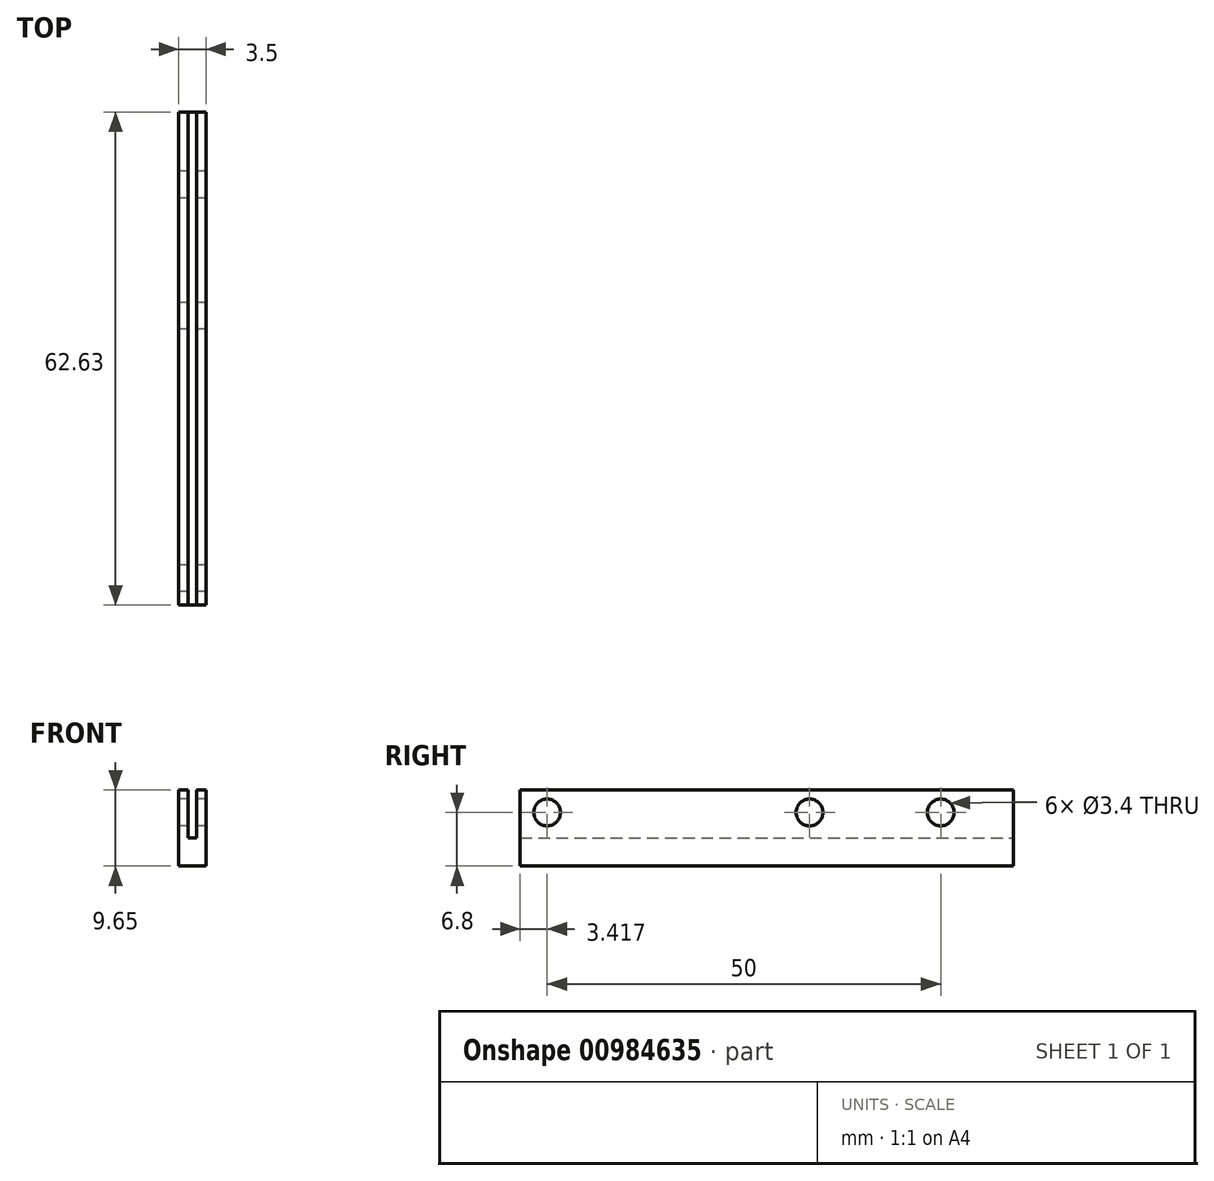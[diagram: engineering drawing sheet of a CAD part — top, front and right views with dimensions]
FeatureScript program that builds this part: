
annotation { "Feature Type Name" : "Feature", "Feature Type Description" : "" }
export const myFeature = defineFeature(function(context is Context, id is Id, definition is map)
    precondition{}
    {
        {
            var Q0;
            Q0=qCreatedBy(makeId("Right.planeOp"),FACE);
            var sketch = newSketch(context, id + "F0", { "sketchPlane" : qUnion([Q0])});
            skLineSegment(sketch, "E0", {"start": v(0, 0) * mm, "end": v(33.33, 0) * mm});
            skPoint(sketch, "E1", {"position": v(16.67, 0) * mm});
            skLineSegment(sketch, "E2", {"start": v(0, 0) * mm, "end": v(-33.33, 0) * mm});
            skLineSegment(sketch, "E3.bottom", {"start": v(-36.75, 2.85) * mm, "end": v(25.88, 2.85) * mm});
            skLineSegment(sketch, "E3.top", {"start": v(-36.75, -6.8) * mm, "end": v(25.88, -6.8) * mm});
            skLineSegment(sketch, "E3.left", {"start": v(-36.75, 2.85) * mm, "end": v(-36.75, -6.8) * mm});
            skLineSegment(sketch, "E3.right", {"start": v(25.88, 2.85) * mm, "end": v(25.88, -6.8) * mm});
            skSolve(sketch);
        }
        {
            var Q0;
            {var subQ0=sQuery(id+"F0.wireOp",EDGE,"E3.bottom");Q0=makeQuery(id+"F0.imprint","IMPRINT",FACE,{"disambiguationData":[TD([[makeQuery(id+"F0.imprint","IMPRINT",EDGE,{"derivedFrom":subQ0}),-1.0]])]});}
            extrude(context, id + "F1", {"entities" : qUnion([Q0]), "depth" : 3.5 * mm, "offsetDistance" : 25 * mm});
        }
        {
            var Q0;
            Q0=makeQuery(id+"F1.opExtrude","SWEPT_FACE",FACE,{"disambiguationData":[OSD([sQuery(id+"F0.wireOp",EDGE,"E3.bottom")])]});
            var sketch = newSketch(context, id + "F2", { "sketchPlane" : qUnion([Q0])});
            skLineSegment(sketch, "E4", {"start": v(1.75, -36.75) * mm, "end": v(1.75, 25.88) * mm});
            skLineSegment(sketch, "E5.bottom", {"start": v(1.2, -36.75) * mm, "end": v(2.3, -36.75) * mm});
            skLineSegment(sketch, "E5.top", {"start": v(1.2, 25.88) * mm, "end": v(2.3, 25.88) * mm});
            skLineSegment(sketch, "E5.left", {"start": v(1.2, -36.75) * mm, "end": v(1.2, 25.88) * mm});
            skLineSegment(sketch, "E5.right", {"start": v(2.3, -36.75) * mm, "end": v(2.3, 25.88) * mm});
            skPoint(sketch, "E6", {"position": v(1.75, -36.75) * mm});
            skSolve(sketch);
        }
        {
            var Q0;
            Q0 = qSketchRegion(id + "F2", true);
            extrude(context, id + "F3", {"entities" : qUnion([Q0]), "operationType" : NewBodyOperationType.REMOVE, "oppositeDirection" : true, "depth" : 6.1 * mm, "offsetDistance" : 25 * mm});
        }
        {
            var Q0;
            Q0=sQuery(id+"F0.wireOp",VERTEX,"E1");
            var Q1;
            Q1=sQuery(id+"F0.wireOp",VERTEX,"E2.end");
            var Q2;
            Q2=sQuery(id+"F0.wireOp",VERTEX,"E0.start");
            var Q3;
            Q3=makeQuery(id+"F1.opExtrude","SWEPT_BODY",BODY,{"disambiguationData":[OSD([sQuery(id+"F0.wireOp",EDGE,"E3.bottom"),sQuery(id+"F0.wireOp",EDGE,"E3.top"),sQuery(id+"F0.wireOp",EDGE,"E3.left"),sQuery(id+"F0.wireOp",EDGE,"E3.right")])]});
            hole(context, id + "F4", {"style" : HoleStyle.SIMPLE, "endStyle" : HoleEndStyle.THROUGH, "oppositeDirection" : true, "standardTappedOrClearance" : lookupTablePath({ "fit" : "Normal", "standard" : "ISO", "size" : "M3", "type" : "Clearance" }), "standardBlindInLast" : lookupTablePath({ "fit" : "Normal", "standard" : "ISO", "engagement" : "75%", "pitch" : "0.5 mm", "size" : "M3", "type" : "Clearance & tapped" }), "holeDiameter" : 3.4 * mm, "majorDiameter" : 5 * mm, "isTappedThrough" : true, "tappedDepth" : 12 * mm, "tapClearance" : 3, "locations" : qUnion([Q0, Q1, Q2]), "scope" : qUnion([Q3])});
        }
    });
